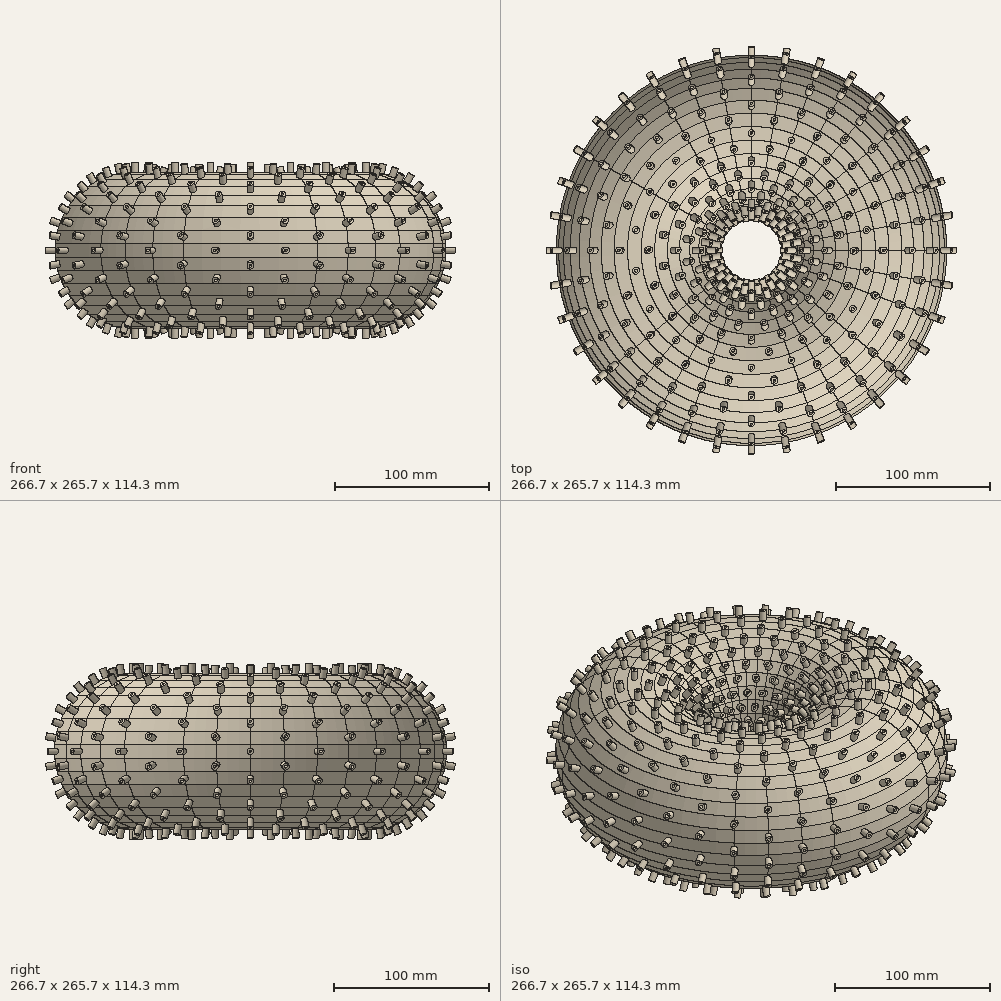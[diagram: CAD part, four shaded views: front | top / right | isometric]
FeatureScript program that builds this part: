
annotation { "Feature Type Name" : "Feature", "Feature Type Description" : "" }
export const myFeature = defineFeature(function(context is Context, id is Id, definition is map)
    precondition{}
    {
        {
            var Q0;
            Q0=qCreatedBy(makeId("Top.planeOp"),FACE);
            var sketch = newSketch(context, id + "F0", { "sketchPlane" : qUnion([Q0])});
            skCircle(sketch, "E0", {"center": v(0, 0) * mm, "radius": 50.8 * mm});
            skSolve(sketch);
        }
        {
            var Q0;
            Q0=qCreatedBy(makeId("Front.planeOp"),FACE);
            cPlane(context, id + "F1", {"entities" : qUnion([Q0]), "cplaneType" : CPlaneType.OFFSET, "offset" : 25.4 * mm, "width" : 152.4 * mm, "height" : 152.4 * mm});
        }
        {
            var Q0;
            Q0=qCreatedBy(id+"F1.planeOp",FACE);
            cPlane(context, id + "F2", {"entities" : qUnion([Q0]), "cplaneType" : CPlaneType.OFFSET, "offset" : 101.6 * mm, "width" : 152.4 * mm, "height" : 152.4 * mm});
        }
        {
            var Q0;
            Q0=qCreatedBy(makeId("Right.planeOp"),FACE);
            var sketch = newSketch(context, id + "F3", { "sketchPlane" : qUnion([Q0])});
            skCircle(sketch, "E1.cCircle", {"center": v(-76.2, 0) * mm, "radius": 50.8 * mm, "construction": true});
            skLineSegment(sketch, "E1.0", {"start": v(-122.42, 21.55) * mm, "end": v(-117.97, 29.25) * mm});
            skLineSegment(sketch, "E1.1", {"start": v(-117.97, 29.25) * mm, "end": v(-112.26, 36.06) * mm});
            skLineSegment(sketch, "E1.2", {"start": v(-112.26, 36.06) * mm, "end": v(-105.45, 41.77) * mm});
            skLineSegment(sketch, "E1.3", {"start": v(-105.45, 41.77) * mm, "end": v(-97.75, 46.22) * mm});
            skLineSegment(sketch, "E1.4", {"start": v(-97.75, 46.22) * mm, "end": v(-89.4, 49.26) * mm});
            skLineSegment(sketch, "E1.5", {"start": v(-89.4, 49.26) * mm, "end": v(-80.64, 50.8) * mm});
            skLineSegment(sketch, "E1.6", {"start": v(-80.64, 50.8) * mm, "end": v(-71.76, 50.8) * mm});
            skLineSegment(sketch, "E1.7", {"start": v(-71.76, 50.8) * mm, "end": v(-63, 49.26) * mm});
            skLineSegment(sketch, "E1.8", {"start": v(-63, 49.26) * mm, "end": v(-54.65, 46.22) * mm});
            skLineSegment(sketch, "E1.9", {"start": v(-54.65, 46.22) * mm, "end": v(-46.95, 41.77) * mm});
            skLineSegment(sketch, "E1.10", {"start": v(-46.95, 41.77) * mm, "end": v(-40.14, 36.06) * mm});
            skLineSegment(sketch, "E1.11", {"start": v(-40.14, 36.06) * mm, "end": v(-34.43, 29.25) * mm});
            skLineSegment(sketch, "E1.12", {"start": v(-34.43, 29.25) * mm, "end": v(-29.98, 21.55) * mm});
            skLineSegment(sketch, "E1.13", {"start": v(-29.98, 21.55) * mm, "end": v(-26.94, 13.2) * mm});
            skLineSegment(sketch, "E1.14", {"start": v(-26.94, 13.2) * mm, "end": v(-25.4, 4.44) * mm});
            skLineSegment(sketch, "E1.15", {"start": v(-25.4, 4.44) * mm, "end": v(-25.4, -4.44) * mm});
            skLineSegment(sketch, "E1.16", {"start": v(-25.4, -4.44) * mm, "end": v(-26.94, -13.2) * mm});
            skLineSegment(sketch, "E1.17", {"start": v(-26.94, -13.2) * mm, "end": v(-29.98, -21.55) * mm});
            skLineSegment(sketch, "E1.18", {"start": v(-29.98, -21.55) * mm, "end": v(-34.43, -29.25) * mm});
            skLineSegment(sketch, "E1.19", {"start": v(-34.43, -29.25) * mm, "end": v(-40.14, -36.06) * mm});
            skLineSegment(sketch, "E1.20", {"start": v(-40.14, -36.06) * mm, "end": v(-46.95, -41.77) * mm});
            skLineSegment(sketch, "E1.21", {"start": v(-46.95, -41.77) * mm, "end": v(-54.65, -46.22) * mm});
            skLineSegment(sketch, "E1.22", {"start": v(-54.65, -46.22) * mm, "end": v(-63, -49.26) * mm});
            skLineSegment(sketch, "E1.23", {"start": v(-63, -49.26) * mm, "end": v(-71.76, -50.8) * mm});
            skLineSegment(sketch, "E1.24", {"start": v(-71.76, -50.8) * mm, "end": v(-80.64, -50.8) * mm});
            skLineSegment(sketch, "E1.25", {"start": v(-80.64, -50.8) * mm, "end": v(-89.4, -49.26) * mm});
            skLineSegment(sketch, "E1.26", {"start": v(-89.4, -49.26) * mm, "end": v(-97.75, -46.22) * mm});
            skLineSegment(sketch, "E1.27", {"start": v(-97.75, -46.22) * mm, "end": v(-105.45, -41.77) * mm});
            skLineSegment(sketch, "E1.28", {"start": v(-105.45, -41.77) * mm, "end": v(-112.26, -36.06) * mm});
            skLineSegment(sketch, "E1.29", {"start": v(-112.26, -36.06) * mm, "end": v(-117.97, -29.25) * mm});
            skLineSegment(sketch, "E1.30", {"start": v(-117.97, -29.25) * mm, "end": v(-122.42, -21.55) * mm});
            skLineSegment(sketch, "E1.31", {"start": v(-122.42, -21.55) * mm, "end": v(-125.46, -13.2) * mm});
            skLineSegment(sketch, "E1.32", {"start": v(-125.46, -13.2) * mm, "end": v(-127, -4.44) * mm});
            skLineSegment(sketch, "E1.33", {"start": v(-127, -4.44) * mm, "end": v(-127, 4.44) * mm});
            skLineSegment(sketch, "E1.34", {"start": v(-127, 4.44) * mm, "end": v(-125.46, 13.2) * mm});
            skLineSegment(sketch, "E1.35", {"start": v(-125.46, 13.2) * mm, "end": v(-122.42, 21.55) * mm});
            skPoint(sketch, "E1.0.midPoint", {"position": v(-120.2, 25.4) * mm});
            skCircle(sketch, "E2.cCircle", {"center": v(-76.2, 0) * mm, "radius": 48.27 * mm, "construction": true});
            skLineSegment(sketch, "E2.0", {"start": v(-124.47, -4.22) * mm, "end": v(-124.47, 4.22) * mm});
            skLineSegment(sketch, "E2.1", {"start": v(-124.47, 4.22) * mm, "end": v(-123, 12.54) * mm});
            skLineSegment(sketch, "E2.2", {"start": v(-123, 12.54) * mm, "end": v(-120.11, 20.48) * mm});
            skLineSegment(sketch, "E2.3", {"start": v(-120.11, 20.48) * mm, "end": v(-115.9, 27.8) * mm});
            skLineSegment(sketch, "E2.4", {"start": v(-115.9, 27.8) * mm, "end": v(-110.46, 34.26) * mm});
            skLineSegment(sketch, "E2.5", {"start": v(-110.46, 34.26) * mm, "end": v(-104, 39.7) * mm});
            skLineSegment(sketch, "E2.6", {"start": v(-104, 39.7) * mm, "end": v(-96.68, 43.91) * mm});
            skLineSegment(sketch, "E2.7", {"start": v(-96.68, 43.91) * mm, "end": v(-88.74, 46.8) * mm});
            skLineSegment(sketch, "E2.8", {"start": v(-88.74, 46.8) * mm, "end": v(-80.42, 48.27) * mm});
            skLineSegment(sketch, "E2.9", {"start": v(-80.42, 48.27) * mm, "end": v(-71.98, 48.27) * mm});
            skLineSegment(sketch, "E2.10", {"start": v(-71.98, 48.27) * mm, "end": v(-63.66, 46.8) * mm});
            skLineSegment(sketch, "E2.11", {"start": v(-63.66, 46.8) * mm, "end": v(-55.72, 43.91) * mm});
            skLineSegment(sketch, "E2.12", {"start": v(-55.72, 43.91) * mm, "end": v(-48.4, 39.7) * mm});
            skLineSegment(sketch, "E2.13", {"start": v(-48.4, 39.7) * mm, "end": v(-41.94, 34.26) * mm});
            skLineSegment(sketch, "E2.14", {"start": v(-41.94, 34.26) * mm, "end": v(-36.5, 27.8) * mm});
            skLineSegment(sketch, "E2.15", {"start": v(-36.5, 27.8) * mm, "end": v(-32.29, 20.48) * mm});
            skLineSegment(sketch, "E2.16", {"start": v(-32.29, 20.48) * mm, "end": v(-29.4, 12.54) * mm});
            skLineSegment(sketch, "E2.17", {"start": v(-29.4, 12.54) * mm, "end": v(-27.93, 4.22) * mm});
            skLineSegment(sketch, "E2.18", {"start": v(-27.93, 4.22) * mm, "end": v(-27.93, -4.22) * mm});
            skLineSegment(sketch, "E2.19", {"start": v(-27.93, -4.22) * mm, "end": v(-29.4, -12.54) * mm});
            skLineSegment(sketch, "E2.20", {"start": v(-29.4, -12.54) * mm, "end": v(-32.29, -20.48) * mm});
            skLineSegment(sketch, "E2.21", {"start": v(-32.29, -20.48) * mm, "end": v(-36.5, -27.8) * mm});
            skLineSegment(sketch, "E2.22", {"start": v(-36.5, -27.8) * mm, "end": v(-41.94, -34.26) * mm});
            skLineSegment(sketch, "E2.23", {"start": v(-41.94, -34.26) * mm, "end": v(-48.4, -39.7) * mm});
            skLineSegment(sketch, "E2.24", {"start": v(-48.4, -39.7) * mm, "end": v(-55.72, -43.91) * mm});
            skLineSegment(sketch, "E2.25", {"start": v(-55.72, -43.91) * mm, "end": v(-63.66, -46.8) * mm});
            skLineSegment(sketch, "E2.26", {"start": v(-63.66, -46.8) * mm, "end": v(-71.98, -48.27) * mm});
            skLineSegment(sketch, "E2.27", {"start": v(-71.98, -48.27) * mm, "end": v(-80.42, -48.27) * mm});
            skLineSegment(sketch, "E2.28", {"start": v(-80.42, -48.27) * mm, "end": v(-88.74, -46.8) * mm});
            skLineSegment(sketch, "E2.29", {"start": v(-88.74, -46.8) * mm, "end": v(-96.68, -43.91) * mm});
            skLineSegment(sketch, "E2.30", {"start": v(-96.68, -43.91) * mm, "end": v(-104, -39.7) * mm});
            skLineSegment(sketch, "E2.31", {"start": v(-104, -39.7) * mm, "end": v(-110.46, -34.26) * mm});
            skLineSegment(sketch, "E2.32", {"start": v(-110.46, -34.26) * mm, "end": v(-115.9, -27.8) * mm});
            skLineSegment(sketch, "E2.33", {"start": v(-115.9, -27.8) * mm, "end": v(-120.11, -20.48) * mm});
            skLineSegment(sketch, "E2.34", {"start": v(-120.11, -20.48) * mm, "end": v(-123, -12.54) * mm});
            skLineSegment(sketch, "E2.35", {"start": v(-123, -12.54) * mm, "end": v(-124.47, -4.22) * mm});
            skPoint(sketch, "E2.0.midPoint", {"position": v(-124.47, 0) * mm});
            skSolve(sketch);
        }
        {
            var Q0;
            Q0=makeQuery(id+"F3.imprint","IMPRINT",FACE,{"disambiguationData":[TD([[makeQuery(id+"F3.imprint","IMPRINT",EDGE,{"derivedFrom":sQuery(id+"F3.wireOp",EDGE,"E1.0")}),-1.0]])]});
            var Q1;
            Q1=sQuery(id+"F0.wireOp",EDGE,"E0");
            revolve(context, id + "F4", {"entities" : qUnion([Q0]), "axis" : qUnion([Q1]), "revolveType" : RevolveType.ONE_DIRECTION, "oppositeDirection" : true, "angle" : 10 * degree});
        }
        {
            var Q0;
            Q0=makeQuery(id+"F4.opRevolve","SWEPT_BODY",BODY,{"disambiguationData":[OSD([sQuery(id+"F3.wireOp",EDGE,"E1.0"),sQuery(id+"F3.wireOp",EDGE,"E1.1"),sQuery(id+"F3.wireOp",EDGE,"E1.2"),sQuery(id+"F3.wireOp",EDGE,"E1.3"),sQuery(id+"F3.wireOp",EDGE,"E1.4"),sQuery(id+"F3.wireOp",EDGE,"E1.5"),sQuery(id+"F3.wireOp",EDGE,"E1.6"),sQuery(id+"F3.wireOp",EDGE,"E1.7"),sQuery(id+"F3.wireOp",EDGE,"E1.8"),sQuery(id+"F3.wireOp",EDGE,"E1.9"),sQuery(id+"F3.wireOp",EDGE,"E1.10"),sQuery(id+"F3.wireOp",EDGE,"E1.11"),sQuery(id+"F3.wireOp",EDGE,"E1.12"),sQuery(id+"F3.wireOp",EDGE,"E1.13"),sQuery(id+"F3.wireOp",EDGE,"E1.14"),sQuery(id+"F3.wireOp",EDGE,"E1.15"),sQuery(id+"F3.wireOp",EDGE,"E1.16"),sQuery(id+"F3.wireOp",EDGE,"E1.17"),sQuery(id+"F3.wireOp",EDGE,"E1.18"),sQuery(id+"F3.wireOp",EDGE,"E1.19"),sQuery(id+"F3.wireOp",EDGE,"E1.20"),sQuery(id+"F3.wireOp",EDGE,"E1.21"),sQuery(id+"F3.wireOp",EDGE,"E1.22"),sQuery(id+"F3.wireOp",EDGE,"E1.23"),sQuery(id+"F3.wireOp",EDGE,"E1.24"),sQuery(id+"F3.wireOp",EDGE,"E1.25"),sQuery(id+"F3.wireOp",EDGE,"E1.26"),sQuery(id+"F3.wireOp",EDGE,"E1.27"),sQuery(id+"F3.wireOp",EDGE,"E1.28"),sQuery(id+"F3.wireOp",EDGE,"E1.29"),sQuery(id+"F3.wireOp",EDGE,"E1.30"),sQuery(id+"F3.wireOp",EDGE,"E1.31"),sQuery(id+"F3.wireOp",EDGE,"E1.32"),sQuery(id+"F3.wireOp",EDGE,"E1.33"),sQuery(id+"F3.wireOp",EDGE,"E1.34"),sQuery(id+"F3.wireOp",EDGE,"E1.35")])]});
            var Q1;
            Q1=sQuery(id+"F0.wireOp",EDGE,"E0");
            circularPattern(context, id + "F5", {"entities" : qUnion([Q0]), "axis" : qUnion([Q1]), "angle" : 10 * degree, "instanceCount" : round(36), "oppositeDirection" : true});
        }
        {
            var Q0;
            Q0=makeQuery(id+"F4.opRevolve","CAP_EDGE",EDGE,{"disambiguationData":[OSD([sQuery(id+"F3.wireOp",EDGE,"E1.34")])],"isStart":true});
            var Q1;
            Q1=sQuery(id+"F0.wireOp",EDGE,"E0");
            cPlane(context, id + "F6", {"entities" : qUnion([Q0, Q1]), "cplaneType" : CPlaneType.LINE_ANGLE, "offset" : 152.4 * mm, "angle" : 90 * degree, "width" : 152.4 * mm, "height" : 152.4 * mm});
        }
        {
            var Q0;
            Q0=qCreatedBy(id+"F6.planeOp",FACE);
            var sketch = newSketch(context, id + "F7", { "sketchPlane" : qUnion([Q0])});
            skCircle(sketch, "E3", {"center": v(0, -13.23) * mm, "radius": 2.22 * mm});
            skCircle(sketch, "E4", {"center": v(0, -13.23) * mm, "radius": 0.95 * mm});
            skSolve(sketch);
        }
        {
            var Q0;
            Q0=makeQuery(id+"F7.imprint","IMPRINT",FACE,{"disambiguationData":[TD([[makeQuery(id+"F7.imprint","IMPRINT",EDGE,{"derivedFrom":sQuery(id+"F7.wireOp",EDGE,"E3")}),1.0]])]});
            extrude(context, id + "F8", {"entities" : qUnion([Q0]), "oppositeDirection" : true, "depth" : 6.35 * mm});
        }
        {
            var Q0;
            Q0=makeQuery(id+"F8.opExtrude","SWEPT_BODY",BODY,{"disambiguationData":[OSD([sQuery(id+"F7.wireOp",EDGE,"E3")])]});
            var Q1;
            Q1=sQuery(id+"F0.wireOp",EDGE,"E0");
            circularPattern(context, id + "F9", {"entities" : qUnion([Q0]), "axis" : qUnion([Q1]), "angle" : 20 * degree, "instanceCount" : round(18), "oppositeDirection" : true});
        }
        {
            var Q0;
            Q0=makeQuery(id+"F5.opPattern","COPY",EDGE,{"derivedFrom":makeQuery(id+"F4.opRevolve","CAP_EDGE",EDGE,{"disambiguationData":[OSD([sQuery(id+"F3.wireOp",EDGE,"E1.35")])],"isStart":true}),"instanceName":"1"});
            var Q1;
            Q1=sQuery(id+"F0.wireOp",EDGE,"E0");
            cPlane(context, id + "F10", {"entities" : qUnion([Q0, Q1]), "cplaneType" : CPlaneType.LINE_ANGLE, "offset" : 152.4 * mm, "angle" : 90 * degree, "width" : 152.4 * mm, "height" : 152.4 * mm});
        }
        {
            var Q0;
            Q0=qCreatedBy(id+"F10.planeOp",FACE);
            var sketch = newSketch(context, id + "F11", { "sketchPlane" : qUnion([Q0])});
            skCircle(sketch, "E5", {"center": v(1.57, -26.01) * mm, "radius": 2.22 * mm});
            skCircle(sketch, "E6", {"center": v(1.57, -26.01) * mm, "radius": 0.95 * mm});
            skSolve(sketch);
        }
        {
            var Q0;
            Q0=makeQuery(id+"F11.imprint","IMPRINT",FACE,{"disambiguationData":[TD([[makeQuery(id+"F11.imprint","IMPRINT",EDGE,{"derivedFrom":sQuery(id+"F11.wireOp",EDGE,"E5")}),1.0]])]});
            extrude(context, id + "F12", {"entities" : qUnion([Q0]), "oppositeDirection" : true, "depth" : 6.35 * mm});
        }
        {
            var Q0;
            Q0=makeQuery(id+"F12.opExtrude","SWEPT_BODY",BODY,{"disambiguationData":[OSD([sQuery(id+"F11.wireOp",EDGE,"E5")])]});
            var Q1;
            Q1=sQuery(id+"F0.wireOp",EDGE,"E0");
            circularPattern(context, id + "F13", {"entities" : qUnion([Q0]), "axis" : qUnion([Q1]), "angle" : 20 * degree, "instanceCount" : round(18)});
        }
        {
            var Q0;
            Q0=makeQuery(id+"F4.opRevolve","CAP_EDGE",EDGE,{"disambiguationData":[OSD([sQuery(id+"F3.wireOp",EDGE,"E1.0")])],"isStart":true});
            var Q1;
            Q1=sQuery(id+"F0.wireOp",EDGE,"E0");
            cPlane(context, id + "F14", {"entities" : qUnion([Q0, Q1]), "cplaneType" : CPlaneType.LINE_ANGLE, "offset" : 152.4 * mm, "angle" : 90 * degree, "width" : 152.4 * mm, "height" : 152.4 * mm});
        }
        {
            var Q0;
            Q0=qCreatedBy(id+"F14.planeOp",FACE);
            var sketch = newSketch(context, id + "F15", { "sketchPlane" : qUnion([Q0])});
            skCircle(sketch, "E7", {"center": v(0, -38.1) * mm, "radius": 2.22 * mm});
            skCircle(sketch, "E8", {"center": v(0, -38.1) * mm, "radius": 0.95 * mm});
            skSolve(sketch);
        }
        {
            var Q0;
            Q0=makeQuery(id+"F15.imprint","IMPRINT",FACE,{"disambiguationData":[TD([[makeQuery(id+"F15.imprint","IMPRINT",EDGE,{"derivedFrom":sQuery(id+"F15.wireOp",EDGE,"E7")}),1.0]])]});
            extrude(context, id + "F16", {"entities" : qUnion([Q0]), "oppositeDirection" : true, "depth" : 6.35 * mm});
        }
        {
            var Q0;
            Q0=makeQuery(id+"F16.opExtrude","SWEPT_BODY",BODY,{"disambiguationData":[OSD([sQuery(id+"F15.wireOp",EDGE,"E7")])]});
            var Q1;
            Q1=sQuery(id+"F0.wireOp",EDGE,"E0");
            circularPattern(context, id + "F17", {"entities" : qUnion([Q0]), "axis" : qUnion([Q1]), "angle" : 20 * degree, "instanceCount" : round(18)});
        }
        {
            var Q0;
            Q0=makeQuery(id+"F5.opPattern","COPY",EDGE,{"derivedFrom":makeQuery(id+"F4.opRevolve","CAP_EDGE",EDGE,{"disambiguationData":[OSD([sQuery(id+"F3.wireOp",EDGE,"E1.1")])],"isStart":false}),"instanceName":"34"});
            var Q1;
            Q1=sQuery(id+"F0.wireOp",EDGE,"E0");
            cPlane(context, id + "F18", {"entities" : qUnion([Q0, Q1]), "cplaneType" : CPlaneType.LINE_ANGLE, "offset" : 152.4 * mm, "angle" : 90 * degree, "width" : 152.4 * mm, "height" : 152.4 * mm});
        }
        {
            var Q0;
            Q0=qCreatedBy(id+"F18.planeOp",FACE);
            var sketch = newSketch(context, id + "F19", { "sketchPlane" : qUnion([Q0])});
            skCircle(sketch, "E9", {"center": v(-5.52, -48.67) * mm, "radius": 2.22 * mm});
            skCircle(sketch, "E10", {"center": v(-5.52, -48.67) * mm, "radius": 0.95 * mm});
            skSolve(sketch);
        }
        {
            var Q0;
            Q0=makeQuery(id+"F19.imprint","IMPRINT",FACE,{"disambiguationData":[TD([[makeQuery(id+"F19.imprint","IMPRINT",EDGE,{"derivedFrom":sQuery(id+"F19.wireOp",EDGE,"E9")}),1.0]])]});
            extrude(context, id + "F20", {"entities" : qUnion([Q0]), "oppositeDirection" : true, "depth" : 6.35 * mm});
        }
        {
            var Q0;
            Q0=makeQuery(id+"F20.opExtrude","SWEPT_BODY",BODY,{"disambiguationData":[OSD([sQuery(id+"F19.wireOp",EDGE,"E9")])]});
            var Q1;
            Q1=sQuery(id+"F0.wireOp",EDGE,"E0");
            circularPattern(context, id + "F21", {"entities" : qUnion([Q0]), "axis" : qUnion([Q1]), "angle" : 20 * degree, "instanceCount" : round(18)});
        }
        {
            var Q0;
            Q0=makeQuery(id+"F4.opRevolve","CAP_EDGE",EDGE,{"disambiguationData":[OSD([sQuery(id+"F3.wireOp",EDGE,"E1.2")])],"isStart":true});
            var Q1;
            Q1=sQuery(id+"F0.wireOp",EDGE,"E0");
            cPlane(context, id + "F22", {"entities" : qUnion([Q0, Q1]), "cplaneType" : CPlaneType.LINE_ANGLE, "offset" : 152.4 * mm, "angle" : 90 * degree, "width" : 152.4 * mm, "height" : 152.4 * mm});
        }
        {
            var Q0;
            Q0=qCreatedBy(id+"F22.planeOp",FACE);
            var sketch = newSketch(context, id + "F23", { "sketchPlane" : qUnion([Q0])});
            skCircle(sketch, "E11", {"center": v(0, 58.37) * mm, "radius": 2.22 * mm});
            skCircle(sketch, "E12", {"center": v(0, 58.37) * mm, "radius": 0.95 * mm});
            skSolve(sketch);
        }
        {
            var Q0;
            Q0=makeQuery(id+"F23.imprint","IMPRINT",FACE,{"disambiguationData":[TD([[makeQuery(id+"F23.imprint","IMPRINT",EDGE,{"derivedFrom":sQuery(id+"F23.wireOp",EDGE,"E11")}),1.0]])]});
            extrude(context, id + "F24", {"entities" : qUnion([Q0]), "oppositeDirection" : true, "depth" : 6.35 * mm});
        }
        {
            var Q0;
            Q0=makeQuery(id+"F24.opExtrude","SWEPT_BODY",BODY,{"disambiguationData":[OSD([sQuery(id+"F23.wireOp",EDGE,"E11")])]});
            var Q1;
            Q1=sQuery(id+"F0.wireOp",EDGE,"E0");
            circularPattern(context, id + "F25", {"entities" : qUnion([Q0]), "axis" : qUnion([Q1]), "angle" : 20 * degree, "instanceCount" : round(18)});
        }
        {
            var Q0;
            Q0=makeQuery(id+"F5.opPattern","COPY",EDGE,{"derivedFrom":makeQuery(id+"F4.opRevolve","CAP_EDGE",EDGE,{"disambiguationData":[OSD([sQuery(id+"F3.wireOp",EDGE,"E1.3")])],"isStart":true}),"instanceName":"1"});
            var Q1;
            Q1=sQuery(id+"F0.wireOp",EDGE,"E0");
            cPlane(context, id + "F26", {"entities" : qUnion([Q0, Q1]), "cplaneType" : CPlaneType.LINE_ANGLE, "offset" : 152.4 * mm, "angle" : 90 * degree, "width" : 152.4 * mm, "height" : 152.4 * mm});
        }
        {
            var Q0;
            Q0=qCreatedBy(id+"F26.planeOp",FACE);
            var sketch = newSketch(context, id + "F27", { "sketchPlane" : qUnion([Q0])});
            skCircle(sketch, "E13", {"center": v(-9.96, 65.23) * mm, "radius": 2.22 * mm});
            skCircle(sketch, "E14", {"center": v(-9.96, 65.23) * mm, "radius": 0.95 * mm});
            skSolve(sketch);
        }
        {
            var Q0;
            Q0=qSketchRegion(id+"F27",true);
            extrude(context, id + "F28", {"entities" : qUnion([Q0]), "oppositeDirection" : true, "depth" : 6.35 * mm});
        }
        {
            var Q0;
            Q0=makeQuery(id+"F28.opExtrude","SWEPT_BODY",BODY,{"disambiguationData":[OSD([sQuery(id+"F27.wireOp",EDGE,"E13")])]});
            var Q1;
            Q1=sQuery(id+"F0.wireOp",EDGE,"E0");
            circularPattern(context, id + "F29", {"entities" : qUnion([Q0]), "axis" : qUnion([Q1]), "angle" : 20 * degree, "instanceCount" : round(18)});
        }
        {
            var Q0;
            Q0=makeQuery(id+"F4.opRevolve","CAP_EDGE",EDGE,{"disambiguationData":[OSD([sQuery(id+"F3.wireOp",EDGE,"E1.4")])],"isStart":true});
            var Q1;
            Q1=sQuery(id+"F0.wireOp",EDGE,"E0");
            cPlane(context, id + "F30", {"entities" : qUnion([Q0, Q1]), "cplaneType" : CPlaneType.LINE_ANGLE, "offset" : 152.4 * mm, "angle" : 90 * degree, "width" : 152.4 * mm, "height" : 152.4 * mm});
        }
        {
            var Q0;
            Q0=qCreatedBy(id+"F30.planeOp",FACE);
            var sketch = newSketch(context, id + "F31", { "sketchPlane" : qUnion([Q0])});
            skCircle(sketch, "E15", {"center": v(0, 71.6) * mm, "radius": 2.22 * mm});
            skCircle(sketch, "E16", {"center": v(0, 71.6) * mm, "radius": 0.95 * mm});
            skSolve(sketch);
        }
        {
            var Q0;
            Q0=qSketchRegion(id+"F31",true);
            extrude(context, id + "F32", {"entities" : qUnion([Q0]), "oppositeDirection" : true, "depth" : 6.35 * mm});
        }
        {
            var Q0;
            Q0=makeQuery(id+"F32.opExtrude","SWEPT_BODY",BODY,{"disambiguationData":[OSD([sQuery(id+"F31.wireOp",EDGE,"E15")])]});
            var Q1;
            Q1=sQuery(id+"F0.wireOp",EDGE,"E0");
            circularPattern(context, id + "F33", {"entities" : qUnion([Q0]), "axis" : qUnion([Q1]), "angle" : 20 * degree, "instanceCount" : round(18)});
        }
        {
            var Q0;
            Q0=makeQuery(id+"F5.opPattern","COPY",EDGE,{"derivedFrom":makeQuery(id+"F4.opRevolve","CAP_EDGE",EDGE,{"disambiguationData":[OSD([sQuery(id+"F3.wireOp",EDGE,"E1.5")])],"isStart":true}),"instanceName":"1"});
            var Q1;
            Q1=sQuery(id+"F0.wireOp",EDGE,"E0");
            cPlane(context, id + "F34", {"entities" : qUnion([Q0, Q1]), "cplaneType" : CPlaneType.LINE_ANGLE, "offset" : 152.4 * mm, "angle" : 90 * degree, "width" : 152.4 * mm, "height" : 152.4 * mm});
        }
        {
            var Q0;
            Q0=qCreatedBy(id+"F34.planeOp",FACE);
            var sketch = newSketch(context, id + "F35", { "sketchPlane" : qUnion([Q0])});
            skCircle(sketch, "E17", {"center": v(-12.84, 73.94) * mm, "radius": 2.22 * mm});
            skCircle(sketch, "E18", {"center": v(-12.84, 73.94) * mm, "radius": 0.95 * mm});
            skSolve(sketch);
        }
        {
            var Q0;
            Q0=qSketchRegion(id+"F35",true);
            extrude(context, id + "F36", {"entities" : qUnion([Q0]), "oppositeDirection" : true, "depth" : 6.35 * mm});
        }
        {
            var Q0;
            Q0=makeQuery(id+"F36.opExtrude","SWEPT_BODY",BODY,{"disambiguationData":[OSD([sQuery(id+"F35.wireOp",EDGE,"E17")])]});
            var Q1;
            Q1=sQuery(id+"F0.wireOp",EDGE,"E0");
            circularPattern(context, id + "F37", {"entities" : qUnion([Q0]), "axis" : qUnion([Q1]), "angle" : 20 * degree, "instanceCount" : round(18)});
        }
        {
            var Q0;
            Q0=makeQuery(id+"F4.opRevolve","CAP_EDGE",EDGE,{"disambiguationData":[OSD([sQuery(id+"F3.wireOp",EDGE,"E1.6")])],"isStart":true});
            var Q1;
            Q1=sQuery(id+"F0.wireOp",EDGE,"E0");
            cPlane(context, id + "F38", {"entities" : qUnion([Q0, Q1]), "cplaneType" : CPlaneType.LINE_ANGLE, "offset" : 152.4 * mm, "angle" : 90 * degree, "width" : 152.4 * mm, "height" : 152.4 * mm});
        }
        {
            var Q0;
            Q0=qCreatedBy(id+"F38.planeOp",FACE);
            var sketch = newSketch(context, id + "F39", { "sketchPlane" : qUnion([Q0])});
            skCircle(sketch, "E19", {"center": v(0, 76.2) * mm, "radius": 2.22 * mm});
            skCircle(sketch, "E20", {"center": v(0, 76.2) * mm, "radius": 0.95 * mm});
            skSolve(sketch);
        }
        {
            var Q0;
            Q0=qSketchRegion(id+"F39",true);
            extrude(context, id + "F40", {"entities" : qUnion([Q0]), "oppositeDirection" : true, "depth" : 6.35 * mm});
        }
        {
            var Q0;
            Q0=makeQuery(id+"F40.opExtrude","SWEPT_BODY",BODY,{"disambiguationData":[OSD([sQuery(id+"F39.wireOp",EDGE,"E19")])]});
            var Q1;
            Q1=sQuery(id+"F0.wireOp",EDGE,"E0");
            circularPattern(context, id + "F41", {"entities" : qUnion([Q0]), "axis" : qUnion([Q1]), "angle" : 20 * degree, "instanceCount" : round(18)});
        }
        {
            var Q0;
            Q0=makeQuery(id+"F5.opPattern","COPY",EDGE,{"derivedFrom":makeQuery(id+"F4.opRevolve","CAP_EDGE",EDGE,{"disambiguationData":[OSD([sQuery(id+"F3.wireOp",EDGE,"E1.7")])],"isStart":false}),"instanceName":"34"});
            var Q1;
            Q1=sQuery(id+"F0.wireOp",EDGE,"E0");
            cPlane(context, id + "F42", {"entities" : qUnion([Q0, Q1]), "cplaneType" : CPlaneType.LINE_ANGLE, "offset" : 152.4 * mm, "angle" : 90 * degree, "width" : 152.4 * mm, "height" : 152.4 * mm});
        }
        {
            var Q0;
            Q0=qCreatedBy(id+"F42.planeOp",FACE);
            var sketch = newSketch(context, id + "F43", { "sketchPlane" : qUnion([Q0])});
            skCircle(sketch, "E21", {"center": v(-10.55, 73.94) * mm, "radius": 2.22 * mm});
            skCircle(sketch, "E22", {"center": v(-10.55, 73.94) * mm, "radius": 0.95 * mm});
            skSolve(sketch);
        }
        {
            var Q0;
            Q0=qSketchRegion(id+"F43",true);
            extrude(context, id + "F44", {"entities" : qUnion([Q0]), "oppositeDirection" : true, "depth" : 6.35 * mm});
        }
        {
            var Q0;
            Q0=makeQuery(id+"F44.opExtrude","SWEPT_BODY",BODY,{"disambiguationData":[OSD([sQuery(id+"F43.wireOp",EDGE,"E21")])]});
            var Q1;
            Q1=sQuery(id+"F0.wireOp",EDGE,"E0");
            circularPattern(context, id + "F45", {"entities" : qUnion([Q0]), "axis" : qUnion([Q1]), "angle" : 20 * degree, "instanceCount" : round(18)});
        }
        {
            var Q0;
            Q0=makeQuery(id+"F4.opRevolve","CAP_EDGE",EDGE,{"disambiguationData":[OSD([sQuery(id+"F3.wireOp",EDGE,"E1.8")])],"isStart":true});
            var Q1;
            Q1=sQuery(id+"F0.wireOp",EDGE,"E0");
            cPlane(context, id + "F46", {"entities" : qUnion([Q0, Q1]), "cplaneType" : CPlaneType.LINE_ANGLE, "offset" : 152.4 * mm, "angle" : 90 * degree, "width" : 152.4 * mm, "height" : 152.4 * mm});
        }
        {
            var Q0;
            Q0=qCreatedBy(id+"F46.planeOp",FACE);
            var sketch = newSketch(context, id + "F47", { "sketchPlane" : qUnion([Q0])});
            skCircle(sketch, "E23", {"center": v(0, 71.6) * mm, "radius": 2.22 * mm});
            skCircle(sketch, "E24", {"center": v(0, 71.6) * mm, "radius": 0.95 * mm});
            skSolve(sketch);
        }
        {
            var Q0;
            Q0=qSketchRegion(id+"F47",true);
            extrude(context, id + "F48", {"entities" : qUnion([Q0]), "oppositeDirection" : true, "depth" : 6.35 * mm});
        }
        {
            var Q0;
            Q0=makeQuery(id+"F48.opExtrude","SWEPT_BODY",BODY,{"disambiguationData":[OSD([sQuery(id+"F47.wireOp",EDGE,"E23")])]});
            var Q1;
            Q1=sQuery(id+"F0.wireOp",EDGE,"E0");
            circularPattern(context, id + "F49", {"entities" : qUnion([Q0]), "axis" : qUnion([Q1]), "angle" : 20 * degree, "instanceCount" : round(18)});
        }
        {
            var Q0;
            Q0=makeQuery(id+"F5.opPattern","COPY",EDGE,{"derivedFrom":makeQuery(id+"F4.opRevolve","CAP_EDGE",EDGE,{"disambiguationData":[OSD([sQuery(id+"F3.wireOp",EDGE,"E1.9")])],"isStart":false}),"instanceName":"6"});
            var Q1;
            Q1=sQuery(id+"F0.wireOp",EDGE,"E0");
            cPlane(context, id + "F50", {"entities" : qUnion([Q0, Q1]), "cplaneType" : CPlaneType.LINE_ANGLE, "offset" : 152.4 * mm, "angle" : 90 * degree, "width" : 152.4 * mm, "height" : 152.4 * mm});
        }
        {
            var Q0;
            Q0=qCreatedBy(id+"F50.planeOp",FACE);
            var sketch = newSketch(context, id + "F51", { "sketchPlane" : qUnion([Q0])});
            skCircle(sketch, "E25", {"center": v(-60.84, 25.57) * mm, "radius": 2.22 * mm});
            skCircle(sketch, "E26", {"center": v(-60.84, 25.57) * mm, "radius": 0.95 * mm});
            skSolve(sketch);
        }
        {
            var Q0;
            Q0=qSketchRegion(id+"F51",true);
            extrude(context, id + "F52", {"entities" : qUnion([Q0]), "oppositeDirection" : true, "depth" : 6.35 * mm});
        }
        {
            var Q0;
            Q0=makeQuery(id+"F52.opExtrude","SWEPT_BODY",BODY,{"disambiguationData":[OSD([sQuery(id+"F51.wireOp",EDGE,"E25")])]});
            var Q1;
            Q1=sQuery(id+"F0.wireOp",EDGE,"E0");
            circularPattern(context, id + "F53", {"entities" : qUnion([Q0]), "axis" : qUnion([Q1]), "angle" : 20 * degree, "instanceCount" : round(18)});
        }
        {
            var Q0;
            Q0=makeQuery(id+"F5.opPattern","COPY",EDGE,{"derivedFrom":makeQuery(id+"F4.opRevolve","CAP_EDGE",EDGE,{"disambiguationData":[OSD([sQuery(id+"F3.wireOp",EDGE,"E1.10")])],"isStart":false}),"instanceName":"7"});
            var Q1;
            Q1=sQuery(id+"F0.wireOp",EDGE,"E0");
            cPlane(context, id + "F54", {"entities" : qUnion([Q0, Q1]), "cplaneType" : CPlaneType.LINE_ANGLE, "offset" : 152.4 * mm, "angle" : 90 * degree, "width" : 152.4 * mm, "height" : 152.4 * mm});
        }
        {
            var Q0;
            Q0=qCreatedBy(id+"F54.planeOp",FACE);
            var sketch = newSketch(context, id + "F55", { "sketchPlane" : qUnion([Q0])});
            skCircle(sketch, "E27", {"center": v(-56.89, 13.1) * mm, "radius": 2.22 * mm});
            skCircle(sketch, "E28", {"center": v(-56.89, 13.1) * mm, "radius": 0.95 * mm});
            skSolve(sketch);
        }
        {
            var Q0;
            Q0=qSketchRegion(id+"F55",true);
            extrude(context, id + "F56", {"entities" : qUnion([Q0]), "oppositeDirection" : true, "depth" : 6.35 * mm});
        }
        {
            var Q0;
            Q0=makeQuery(id+"F56.opExtrude","SWEPT_BODY",BODY,{"disambiguationData":[OSD([sQuery(id+"F55.wireOp",EDGE,"E27")])]});
            var Q1;
            Q1=sQuery(id+"F0.wireOp",EDGE,"E0");
            circularPattern(context, id + "F57", {"entities" : qUnion([Q0]), "axis" : qUnion([Q1]), "angle" : 20 * degree, "instanceCount" : round(18)});
        }
        {
            var Q0;
            Q0=makeQuery(id+"F5.opPattern","COPY",EDGE,{"derivedFrom":makeQuery(id+"F4.opRevolve","CAP_EDGE",EDGE,{"disambiguationData":[OSD([sQuery(id+"F3.wireOp",EDGE,"E1.11")])],"isStart":false}),"instanceName":"8"});
            var Q1;
            Q1=sQuery(id+"F0.wireOp",EDGE,"E0");
            cPlane(context, id + "F58", {"entities" : qUnion([Q0, Q1]), "cplaneType" : CPlaneType.LINE_ANGLE, "offset" : 152.4 * mm, "angle" : 90 * degree, "width" : 152.4 * mm, "height" : 152.4 * mm});
        }
        {
            var Q0;
            Q0=qCreatedBy(id+"F58.planeOp",FACE);
            var sketch = newSketch(context, id + "F59", { "sketchPlane" : qUnion([Q0])});
            skCircle(sketch, "E29", {"center": v(0, 48.98) * mm, "radius": 2.22 * mm});
            skCircle(sketch, "E30", {"center": v(0, 48.98) * mm, "radius": 0.95 * mm});
            skSolve(sketch);
        }
        {
            var Q0;
            Q0=qSketchRegion(id+"F59",true);
            extrude(context, id + "F60", {"entities" : qUnion([Q0]), "oppositeDirection" : true, "depth" : 6.35 * mm});
        }
        {
            var Q0;
            Q0=makeQuery(id+"F60.opExtrude","SWEPT_BODY",BODY,{"disambiguationData":[OSD([sQuery(id+"F59.wireOp",EDGE,"E29")])]});
            var Q1;
            Q1=sQuery(id+"F0.wireOp",EDGE,"E0");
            circularPattern(context, id + "F61", {"entities" : qUnion([Q0]), "axis" : qUnion([Q1]), "angle" : 20 * degree, "instanceCount" : round(18)});
        }
        {
            var Q0;
            Q0=makeQuery(id+"F5.opPattern","COPY",EDGE,{"derivedFrom":makeQuery(id+"F4.opRevolve","CAP_EDGE",EDGE,{"disambiguationData":[OSD([sQuery(id+"F3.wireOp",EDGE,"E1.12")])],"isStart":false}),"instanceName":"5"});
            var Q1;
            Q1=sQuery(id+"F0.wireOp",EDGE,"E0");
            cPlane(context, id + "F62", {"entities" : qUnion([Q0, Q1]), "cplaneType" : CPlaneType.LINE_ANGLE, "offset" : 152.4 * mm, "angle" : 90 * degree, "width" : 152.4 * mm, "height" : 152.4 * mm});
        }
        {
            var Q0;
            Q0=qCreatedBy(id+"F62.planeOp",FACE);
            var sketch = newSketch(context, id + "F63", { "sketchPlane" : qUnion([Q0])});
            skCircle(sketch, "E31", {"center": v(10.57, 36.6) * mm, "radius": 2.22 * mm});
            skCircle(sketch, "E32", {"center": v(10.57, 36.6) * mm, "radius": 0.95 * mm});
            skSolve(sketch);
        }
        {
            var Q0;
            Q0=qSketchRegion(id+"F63",true);
            extrude(context, id + "F64", {"entities" : qUnion([Q0]), "oppositeDirection" : true, "depth" : 6.35 * mm});
        }
        {
            var Q0;
            Q0=makeQuery(id+"F64.opExtrude","SWEPT_BODY",BODY,{"disambiguationData":[OSD([sQuery(id+"F63.wireOp",EDGE,"E31")])]});
            var Q1;
            Q1=sQuery(id+"F0.wireOp",EDGE,"E0");
            circularPattern(context, id + "F65", {"entities" : qUnion([Q0]), "axis" : qUnion([Q1]), "angle" : 20 * degree, "instanceCount" : round(18)});
        }
        {
            var Q0;
            Q0=makeQuery(id+"F5.opPattern","COPY",EDGE,{"derivedFrom":makeQuery(id+"F4.opRevolve","CAP_EDGE",EDGE,{"disambiguationData":[OSD([sQuery(id+"F3.wireOp",EDGE,"E1.13")])],"isStart":false}),"instanceName":"8"});
            var Q1;
            Q1=sQuery(id+"F0.wireOp",EDGE,"E0");
            cPlane(context, id + "F66", {"entities" : qUnion([Q0, Q1]), "cplaneType" : CPlaneType.LINE_ANGLE, "offset" : 152.4 * mm, "angle" : 90 * degree, "width" : 152.4 * mm, "height" : 152.4 * mm});
        }
        {
            var Q0;
            Q0=qCreatedBy(id+"F66.planeOp",FACE);
            var sketch = newSketch(context, id + "F67", { "sketchPlane" : qUnion([Q0])});
            skCircle(sketch, "E33", {"center": v(0, 26.06) * mm, "radius": 2.22 * mm});
            skCircle(sketch, "E34", {"center": v(0, 26.06) * mm, "radius": 0.95 * mm});
            skSolve(sketch);
        }
        {
            var Q0;
            Q0=qSketchRegion(id+"F67",true);
            extrude(context, id + "F68", {"entities" : qUnion([Q0]), "oppositeDirection" : true, "depth" : 6.35 * mm});
        }
        {
            var Q0;
            Q0=makeQuery(id+"F68.opExtrude","SWEPT_BODY",BODY,{"disambiguationData":[OSD([sQuery(id+"F67.wireOp",EDGE,"E33")])]});
            var Q1;
            Q1=sQuery(id+"F0.wireOp",EDGE,"E0");
            circularPattern(context, id + "F69", {"entities" : qUnion([Q0]), "axis" : qUnion([Q1]), "angle" : 20 * degree, "instanceCount" : round(18)});
        }
        {
            var Q0;
            Q0=makeQuery(id+"F5.opPattern","COPY",EDGE,{"derivedFrom":makeQuery(id+"F4.opRevolve","CAP_EDGE",EDGE,{"disambiguationData":[OSD([sQuery(id+"F3.wireOp",EDGE,"E1.14")])],"isStart":false}),"instanceName":"7"});
            var Q1;
            Q1=sQuery(id+"F0.wireOp",EDGE,"E0");
            cPlane(context, id + "F70", {"entities" : qUnion([Q0, Q1]), "cplaneType" : CPlaneType.LINE_ANGLE, "offset" : 152.4 * mm, "angle" : 90 * degree, "width" : 152.4 * mm, "height" : 152.4 * mm});
        }
        {
            var Q0;
            Q0=qCreatedBy(id+"F70.planeOp",FACE);
            var sketch = newSketch(context, id + "F71", { "sketchPlane" : qUnion([Q0])});
            skCircle(sketch, "E35", {"center": v(0.4, 13.23) * mm, "radius": 2.22 * mm});
            skCircle(sketch, "E36", {"center": v(0.4, 13.23) * mm, "radius": 0.95 * mm});
            skSolve(sketch);
        }
        {
            var Q0;
            Q0=qSketchRegion(id+"F71",true);
            extrude(context, id + "F72", {"entities" : qUnion([Q0]), "oppositeDirection" : true, "depth" : 6.35 * mm});
        }
        {
            var Q0;
            Q0=makeQuery(id+"F72.opExtrude","SWEPT_BODY",BODY,{"disambiguationData":[OSD([sQuery(id+"F71.wireOp",EDGE,"E35")])]});
            var Q1;
            Q1=sQuery(id+"F0.wireOp",EDGE,"E0");
            circularPattern(context, id + "F73", {"entities" : qUnion([Q0]), "axis" : qUnion([Q1]), "angle" : 20 * degree, "instanceCount" : round(18)});
        }
        {
            var Q0;
            Q0=makeQuery(id+"F5.opPattern","COPY",EDGE,{"derivedFrom":makeQuery(id+"F4.opRevolve","CAP_EDGE",EDGE,{"disambiguationData":[OSD([sQuery(id+"F3.wireOp",EDGE,"E1.15")])],"isStart":false}),"instanceName":"8"});
            var Q1;
            Q1=sQuery(id+"F0.wireOp",EDGE,"E0");
            cPlane(context, id + "F74", {"entities" : qUnion([Q0, Q1]), "cplaneType" : CPlaneType.LINE_ANGLE, "offset" : 152.4 * mm, "angle" : 90 * degree, "width" : 152.4 * mm, "height" : 152.4 * mm});
        }
        {
            var Q0;
            Q0=qCreatedBy(id+"F74.planeOp",FACE);
            var sketch = newSketch(context, id + "F75", { "sketchPlane" : qUnion([Q0])});
            skCircle(sketch, "E37", {"center": v(0, 0) * mm, "radius": 2.22 * mm});
            skCircle(sketch, "E38", {"center": v(0, 0) * mm, "radius": 0.95 * mm});
            skSolve(sketch);
        }
        {
            var Q0;
            Q0=qSketchRegion(id+"F75",true);
            extrude(context, id + "F76", {"entities" : qUnion([Q0]), "oppositeDirection" : true, "depth" : 6.35 * mm});
        }
        {
            var Q0;
            Q0=makeQuery(id+"F76.opExtrude","SWEPT_BODY",BODY,{"disambiguationData":[OSD([sQuery(id+"F75.wireOp",EDGE,"E37")])]});
            var Q1;
            Q1=sQuery(id+"F0.wireOp",EDGE,"E0");
            circularPattern(context, id + "F77", {"entities" : qUnion([Q0]), "axis" : qUnion([Q1]), "angle" : 20 * degree, "instanceCount" : round(18)});
        }
        {
            var Q0;
            Q0=makeQuery(id+"F5.opPattern","COPY",EDGE,{"derivedFrom":makeQuery(id+"F4.opRevolve","CAP_EDGE",EDGE,{"disambiguationData":[OSD([sQuery(id+"F3.wireOp",EDGE,"E1.16")])],"isStart":true}),"instanceName":"10"});
            var Q1;
            Q1=sQuery(id+"F0.wireOp",EDGE,"E0");
            cPlane(context, id + "F78", {"entities" : qUnion([Q0, Q1]), "cplaneType" : CPlaneType.LINE_ANGLE, "offset" : 152.4 * mm, "angle" : 90 * degree, "width" : 152.4 * mm, "height" : 152.4 * mm});
        }
        {
            var Q0;
            Q0=qCreatedBy(id+"F78.planeOp",FACE);
            var sketch = newSketch(context, id + "F79", { "sketchPlane" : qUnion([Q0])});
            skCircle(sketch, "E39", {"center": v(0.4, -13.23) * mm, "radius": 2.22 * mm});
            skCircle(sketch, "E40", {"center": v(0.4, -13.23) * mm, "radius": 0.95 * mm});
            skSolve(sketch);
        }
        {
            var Q0;
            Q0=qSketchRegion(id+"F79",true);
            extrude(context, id + "F80", {"entities" : qUnion([Q0]), "depth" : 6.35 * mm});
        }
        {
            var Q0;
            Q0=makeQuery(id+"F80.opExtrude","SWEPT_BODY",BODY,{"disambiguationData":[OSD([sQuery(id+"F79.wireOp",EDGE,"E39")])]});
            var Q1;
            Q1=sQuery(id+"F0.wireOp",EDGE,"E0");
            circularPattern(context, id + "F81", {"entities" : qUnion([Q0]), "axis" : qUnion([Q1]), "angle" : 20 * degree, "instanceCount" : round(18)});
        }
        {
            var Q0;
            Q0=makeQuery(id+"F5.opPattern","COPY",EDGE,{"derivedFrom":makeQuery(id+"F4.opRevolve","CAP_EDGE",EDGE,{"disambiguationData":[OSD([sQuery(id+"F3.wireOp",EDGE,"E1.17")])],"isStart":true}),"instanceName":"11"});
            var Q1;
            Q1=sQuery(id+"F0.wireOp",EDGE,"E0");
            cPlane(context, id + "F82", {"entities" : qUnion([Q0, Q1]), "cplaneType" : CPlaneType.LINE_ANGLE, "offset" : 152.4 * mm, "angle" : 90 * degree, "width" : 152.4 * mm, "height" : 152.4 * mm});
        }
        {
            var Q0;
            Q0=qCreatedBy(id+"F82.planeOp",FACE);
            var sketch = newSketch(context, id + "F83", { "sketchPlane" : qUnion([Q0])});
            skCircle(sketch, "E41", {"center": v(3.22, -25.86) * mm, "radius": 2.22 * mm});
            skCircle(sketch, "E42", {"center": v(3.22, -25.86) * mm, "radius": 0.95 * mm});
            skSolve(sketch);
        }
        {
            var Q0;
            Q0=qSketchRegion(id+"F83",true);
            extrude(context, id + "F84", {"entities" : qUnion([Q0]), "depth" : 6.35 * mm});
        }
        {
            var Q0;
            Q0=makeQuery(id+"F84.opExtrude","SWEPT_BODY",BODY,{"disambiguationData":[OSD([sQuery(id+"F83.wireOp",EDGE,"E41")])]});
            var Q1;
            Q1=sQuery(id+"F0.wireOp",EDGE,"E0");
            circularPattern(context, id + "F85", {"entities" : qUnion([Q0]), "axis" : qUnion([Q1]), "angle" : 20 * degree, "instanceCount" : round(18)});
        }
        {
            var Q0;
            Q0=makeQuery(id+"F5.opPattern","COPY",EDGE,{"derivedFrom":makeQuery(id+"F4.opRevolve","CAP_EDGE",EDGE,{"disambiguationData":[OSD([sQuery(id+"F3.wireOp",EDGE,"E1.33")])],"isStart":true}),"instanceName":"13"});
            var Q1;
            Q1=sQuery(id+"F0.wireOp",EDGE,"E0");
            cPlane(context, id + "F86", {"entities" : qUnion([Q0, Q1]), "cplaneType" : CPlaneType.LINE_ANGLE, "offset" : 152.4 * mm, "angle" : 90 * degree, "width" : 152.4 * mm, "height" : 152.4 * mm});
        }
        {
            var Q0;
            Q0=qCreatedBy(id+"F86.planeOp",FACE);
            var sketch = newSketch(context, id + "F87", { "sketchPlane" : qUnion([Q0])});
            skCircle(sketch, "E43", {"center": v(0, 0) * mm, "radius": 2.22 * mm});
            skCircle(sketch, "E44", {"center": v(0, 0) * mm, "radius": 0.95 * mm});
            skSolve(sketch);
        }
        {
            var Q0;
            Q0=qSketchRegion(id+"F87",true);
            extrude(context, id + "F88", {"entities" : qUnion([Q0]), "depth" : 6.35 * mm});
        }
        {
            var Q0;
            Q0=makeQuery(id+"F88.opExtrude","SWEPT_BODY",BODY,{"disambiguationData":[OSD([sQuery(id+"F87.wireOp",EDGE,"E43")])]});
            var Q1;
            Q1=sQuery(id+"F0.wireOp",EDGE,"E0");
            circularPattern(context, id + "F89", {"entities" : qUnion([Q0]), "axis" : qUnion([Q1]), "angle" : 20 * degree, "instanceCount" : round(18)});
        }
        {
            var Q0;
            Q0=makeQuery(id+"F5.opPattern","COPY",EDGE,{"derivedFrom":makeQuery(id+"F4.opRevolve","CAP_EDGE",EDGE,{"disambiguationData":[OSD([sQuery(id+"F3.wireOp",EDGE,"E1.32")])],"isStart":false}),"instanceName":"13"});
            var Q1;
            Q1=sQuery(id+"F0.wireOp",EDGE,"E0");
            cPlane(context, id + "F90", {"entities" : qUnion([Q0, Q1]), "cplaneType" : CPlaneType.LINE_ANGLE, "offset" : 152.4 * mm, "angle" : 90 * degree, "width" : 152.4 * mm, "height" : 152.4 * mm});
        }
        {
            var Q0;
            Q0=qCreatedBy(id+"F90.planeOp",FACE);
            var sketch = newSketch(context, id + "F91", { "sketchPlane" : qUnion([Q0])});
            skCircle(sketch, "E45", {"center": v(1.9, 13.1) * mm, "radius": 2.22 * mm});
            skCircle(sketch, "E46", {"center": v(1.9, 13.1) * mm, "radius": 0.95 * mm});
            skSolve(sketch);
        }
        {
            var Q0;
            Q0=qSketchRegion(id+"F91",true);
            extrude(context, id + "F92", {"entities" : qUnion([Q0]), "depth" : 6.35 * mm});
        }
        {
            var Q0;
            Q0=makeQuery(id+"F92.opExtrude","SWEPT_BODY",BODY,{"disambiguationData":[OSD([sQuery(id+"F91.wireOp",EDGE,"E45")])]});
            var Q1;
            Q1=sQuery(id+"F0.wireOp",EDGE,"E0");
            circularPattern(context, id + "F93", {"entities" : qUnion([Q0]), "axis" : qUnion([Q1]), "angle" : 20 * degree, "instanceCount" : round(18)});
        }
        {
            var Q0;
            Q0=makeQuery(id+"F5.opPattern","COPY",EDGE,{"derivedFrom":makeQuery(id+"F4.opRevolve","CAP_EDGE",EDGE,{"disambiguationData":[OSD([sQuery(id+"F3.wireOp",EDGE,"E1.31")])],"isStart":true}),"instanceName":"13"});
            var Q1;
            Q1=sQuery(id+"F0.wireOp",EDGE,"E0");
            cPlane(context, id + "F94", {"entities" : qUnion([Q0, Q1]), "cplaneType" : CPlaneType.LINE_ANGLE, "offset" : 152.4 * mm, "angle" : 90 * degree, "width" : 152.4 * mm, "height" : 152.4 * mm});
        }
        {
            var Q0;
            Q0=qCreatedBy(id+"F94.planeOp",FACE);
            var sketch = newSketch(context, id + "F95", { "sketchPlane" : qUnion([Q0])});
            skCircle(sketch, "E47", {"center": v(-7.19, 25.05) * mm, "radius": 2.22 * mm});
            skCircle(sketch, "E48", {"center": v(-7.19, 25.05) * mm, "radius": 0.95 * mm});
            skSolve(sketch);
        }
        {
            var Q0;
            Q0=qSketchRegion(id+"F95",true);
            extrude(context, id + "F96", {"entities" : qUnion([Q0]), "depth" : 6.35 * mm});
        }
        {
            var Q0;
            Q0=makeQuery(id+"F96.opExtrude","SWEPT_BODY",BODY,{"disambiguationData":[OSD([sQuery(id+"F95.wireOp",EDGE,"E47")])]});
            var Q1;
            Q1=sQuery(id+"F0.wireOp",EDGE,"E0");
            circularPattern(context, id + "F97", {"entities" : qUnion([Q0]), "axis" : qUnion([Q1]), "angle" : 20 * degree, "instanceCount" : round(18)});
        }
        {
            var Q0;
            Q0=makeQuery(id+"F5.opPattern","COPY",EDGE,{"derivedFrom":makeQuery(id+"F4.opRevolve","CAP_EDGE",EDGE,{"disambiguationData":[OSD([sQuery(id+"F3.wireOp",EDGE,"E1.30")])],"isStart":false}),"instanceName":"13"});
            var Q1;
            Q1=sQuery(id+"F0.wireOp",EDGE,"E0");
            cPlane(context, id + "F98", {"entities" : qUnion([Q0, Q1]), "cplaneType" : CPlaneType.LINE_ANGLE, "offset" : 152.4 * mm, "angle" : 90 * degree, "width" : 152.4 * mm, "height" : 152.4 * mm});
        }
        {
            var Q0;
            Q0=qCreatedBy(id+"F98.planeOp",FACE);
            var sketch = newSketch(context, id + "F99", { "sketchPlane" : qUnion([Q0])});
            skCircle(sketch, "E49", {"center": v(14.74, 35.13) * mm, "radius": 2.22 * mm});
            skCircle(sketch, "E50", {"center": v(14.74, 35.13) * mm, "radius": 0.95 * mm});
            skSolve(sketch);
        }
        {
            var Q0;
            Q0=qSketchRegion(id+"F99",true);
            extrude(context, id + "F100", {"entities" : qUnion([Q0]), "depth" : 6.35 * mm});
        }
        {
            var Q0;
            Q0=makeQuery(id+"F100.opExtrude","SWEPT_BODY",BODY,{"disambiguationData":[OSD([sQuery(id+"F99.wireOp",EDGE,"E49")])]});
            var Q1;
            Q1=sQuery(id+"F0.wireOp",EDGE,"E0");
            circularPattern(context, id + "F101", {"entities" : qUnion([Q0]), "axis" : qUnion([Q1]), "angle" : 20 * degree, "instanceCount" : round(18)});
        }
        {
            var Q0;
            Q0=makeQuery(id+"F5.opPattern","COPY",EDGE,{"derivedFrom":makeQuery(id+"F4.opRevolve","CAP_EDGE",EDGE,{"disambiguationData":[OSD([sQuery(id+"F3.wireOp",EDGE,"E1.29")])],"isStart":true}),"instanceName":"13"});
            var Q1;
            Q1=sQuery(id+"F0.wireOp",EDGE,"E0");
            cPlane(context, id + "F102", {"entities" : qUnion([Q0, Q1]), "cplaneType" : CPlaneType.LINE_ANGLE, "offset" : 152.4 * mm, "angle" : 90 * degree, "width" : 152.4 * mm, "height" : 152.4 * mm});
        }
        {
            var Q0;
            Q0=qCreatedBy(id+"F102.planeOp",FACE);
            var sketch = newSketch(context, id + "F103", { "sketchPlane" : qUnion([Q0])});
            skCircle(sketch, "E51", {"center": v(-29.79, -38.88) * mm, "radius": 2.22 * mm});
            skCircle(sketch, "E52", {"center": v(-29.79, -38.88) * mm, "radius": 0.95 * mm});
            skSolve(sketch);
        }
        {
            var Q0;
            Q0=qSketchRegion(id+"F103",true);
            extrude(context, id + "F104", {"entities" : qUnion([Q0]), "depth" : 6.35 * mm});
        }
        {
            var Q0;
            Q0=makeQuery(id+"F104.opExtrude","SWEPT_BODY",BODY,{"disambiguationData":[OSD([sQuery(id+"F103.wireOp",EDGE,"E51")])]});
            var Q1;
            Q1=sQuery(id+"F0.wireOp",EDGE,"E0");
            circularPattern(context, id + "F105", {"entities" : qUnion([Q0]), "axis" : qUnion([Q1]), "angle" : 20 * degree, "instanceCount" : round(18)});
        }
        {
            var Q0;
            Q0=makeQuery(id+"F5.opPattern","COPY",EDGE,{"derivedFrom":makeQuery(id+"F4.opRevolve","CAP_EDGE",EDGE,{"disambiguationData":[OSD([sQuery(id+"F3.wireOp",EDGE,"E1.28")])],"isStart":false}),"instanceName":"13"});
            var Q1;
            Q1=sQuery(id+"F0.wireOp",EDGE,"E0");
            cPlane(context, id + "F106", {"entities" : qUnion([Q0, Q1]), "cplaneType" : CPlaneType.LINE_ANGLE, "offset" : 152.4 * mm, "angle" : 90 * degree, "width" : 152.4 * mm, "height" : 152.4 * mm});
        }
        {
            var Q0;
            Q0=qCreatedBy(id+"F106.planeOp",FACE);
            var sketch = newSketch(context, id + "F107", { "sketchPlane" : qUnion([Q0])});
            skCircle(sketch, "E53", {"center": v(-31.56, -49.1) * mm, "radius": 2.22 * mm});
            skCircle(sketch, "E54", {"center": v(-31.56, -49.1) * mm, "radius": 0.95 * mm});
            skSolve(sketch);
        }
        {
            var Q0;
            Q0=qSketchRegion(id+"F107",true);
            extrude(context, id + "F108", {"entities" : qUnion([Q0]), "depth" : 6.35 * mm});
        }
        {
            var Q0;
            Q0=makeQuery(id+"F108.opExtrude","SWEPT_BODY",BODY,{"disambiguationData":[OSD([sQuery(id+"F107.wireOp",EDGE,"E53")])]});
            var Q1;
            Q1=sQuery(id+"F0.wireOp",EDGE,"E0");
            circularPattern(context, id + "F109", {"entities" : qUnion([Q0]), "axis" : qUnion([Q1]), "angle" : 20 * degree, "instanceCount" : round(18)});
        }
        {
            var Q0;
            Q0=makeQuery(id+"F5.opPattern","COPY",EDGE,{"derivedFrom":makeQuery(id+"F4.opRevolve","CAP_EDGE",EDGE,{"disambiguationData":[OSD([sQuery(id+"F3.wireOp",EDGE,"E1.27")])],"isStart":true}),"instanceName":"11"});
            var Q1;
            Q1=sQuery(id+"F0.wireOp",EDGE,"E0");
            cPlane(context, id + "F110", {"entities" : qUnion([Q0, Q1]), "cplaneType" : CPlaneType.LINE_ANGLE, "offset" : 152.4 * mm, "angle" : 90 * degree, "width" : 152.4 * mm, "height" : 152.4 * mm});
        }
        {
            var Q0;
            Q0=qCreatedBy(id+"F110.planeOp",FACE);
            var sketch = newSketch(context, id + "F111", { "sketchPlane" : qUnion([Q0])});
            skCircle(sketch, "E55", {"center": v(-60.84, -25.57) * mm, "radius": 2.22 * mm});
            skCircle(sketch, "E56", {"center": v(-60.84, -25.57) * mm, "radius": 0.95 * mm});
            skSolve(sketch);
        }
        {
            var Q0;
            Q0=qSketchRegion(id+"F111",true);
            extrude(context, id + "F112", {"entities" : qUnion([Q0]), "depth" : 6.35 * mm});
        }
        {
            var Q0;
            Q0=makeQuery(id+"F112.opExtrude","SWEPT_BODY",BODY,{"disambiguationData":[OSD([sQuery(id+"F111.wireOp",EDGE,"E55")])]});
            var Q1;
            Q1=sQuery(id+"F0.wireOp",EDGE,"E0");
            circularPattern(context, id + "F113", {"entities" : qUnion([Q0]), "axis" : qUnion([Q1]), "angle" : 20 * degree, "instanceCount" : round(18)});
        }
        {
            var Q0;
            Q0=makeQuery(id+"F5.opPattern","COPY",EDGE,{"derivedFrom":makeQuery(id+"F4.opRevolve","CAP_EDGE",EDGE,{"disambiguationData":[OSD([sQuery(id+"F3.wireOp",EDGE,"E1.26")])],"isStart":true}),"instanceName":"30"});
            var Q1;
            Q1=sQuery(id+"F0.wireOp",EDGE,"E0");
            cPlane(context, id + "F114", {"entities" : qUnion([Q0, Q1]), "cplaneType" : CPlaneType.LINE_ANGLE, "offset" : 152.4 * mm, "angle" : 90 * degree, "width" : 152.4 * mm, "height" : 152.4 * mm});
        }
        {
            var Q0;
            Q0=qCreatedBy(id+"F114.planeOp",FACE);
            var sketch = newSketch(context, id + "F115", { "sketchPlane" : qUnion([Q0])});
            skCircle(sketch, "E57", {"center": v(61, 37.48) * mm, "radius": 2.22 * mm});
            skCircle(sketch, "E58", {"center": v(61, 37.48) * mm, "radius": 0.95 * mm});
            skSolve(sketch);
        }
        {
            var Q0;
            Q0=makeQuery(id+"F115.imprint","IMPRINT",FACE,{"disambiguationData":[TD([[makeQuery(id+"F115.imprint","IMPRINT",EDGE,{"derivedFrom":sQuery(id+"F115.wireOp",EDGE,"E57")}),1.0]])]});
            extrude(context, id + "F116", {"entities" : qUnion([Q0]), "depth" : 6.35 * mm});
        }
        {
            var Q0;
            Q0=makeQuery(id+"F116.opExtrude","SWEPT_BODY",BODY,{"disambiguationData":[OSD([sQuery(id+"F115.wireOp",EDGE,"E57")])]});
            var Q1;
            Q1=sQuery(id+"F0.wireOp",EDGE,"E0");
            circularPattern(context, id + "F117", {"entities" : qUnion([Q0]), "axis" : qUnion([Q1]), "angle" : 20 * degree, "instanceCount" : round(18)});
        }
        {
            var Q0;
            Q0=makeQuery(id+"F5.opPattern","COPY",EDGE,{"derivedFrom":makeQuery(id+"F4.opRevolve","CAP_EDGE",EDGE,{"disambiguationData":[OSD([sQuery(id+"F3.wireOp",EDGE,"E1.25")])],"isStart":false}),"instanceName":"6"});
            var Q1;
            Q1=sQuery(id+"F0.wireOp",EDGE,"E0");
            cPlane(context, id + "F118", {"entities" : qUnion([Q0, Q1]), "cplaneType" : CPlaneType.LINE_ANGLE, "offset" : 152.4 * mm, "angle" : 90 * degree, "width" : 152.4 * mm, "height" : 152.4 * mm});
        }
        {
            var Q0;
            Q0=qCreatedBy(id+"F118.planeOp",FACE);
            var sketch = newSketch(context, id + "F119", { "sketchPlane" : qUnion([Q0])});
            skCircle(sketch, "E59", {"center": v(-70.39, 26.01) * mm, "radius": 2.22 * mm});
            skCircle(sketch, "E60", {"center": v(-70.39, 26.01) * mm, "radius": 0.95 * mm});
            skSolve(sketch);
        }
        {
            var Q0;
            Q0=qSketchRegion(id+"F119",true);
            extrude(context, id + "F120", {"entities" : qUnion([Q0]), "depth" : 6.35 * mm});
        }
        {
            var Q0;
            Q0=makeQuery(id+"F120.opExtrude","SWEPT_BODY",BODY,{"disambiguationData":[OSD([sQuery(id+"F119.wireOp",EDGE,"E59")])]});
            var Q1;
            Q1=sQuery(id+"F0.wireOp",EDGE,"E0");
            circularPattern(context, id + "F121", {"entities" : qUnion([Q0]), "axis" : qUnion([Q1]), "angle" : 20 * degree, "instanceCount" : round(18)});
        }
        {
            var Q0;
            Q0=makeQuery(id+"F5.opPattern","COPY",EDGE,{"derivedFrom":makeQuery(id+"F4.opRevolve","CAP_EDGE",EDGE,{"disambiguationData":[OSD([sQuery(id+"F3.wireOp",EDGE,"E1.24")])],"isStart":false}),"instanceName":"5"});
            var Q1;
            Q1=sQuery(id+"F0.wireOp",EDGE,"E0");
            cPlane(context, id + "F122", {"entities" : qUnion([Q0, Q1]), "cplaneType" : CPlaneType.LINE_ANGLE, "offset" : 152.4 * mm, "angle" : 90 * degree, "width" : 152.4 * mm, "height" : 152.4 * mm});
        }
        {
            var Q0;
            Q0=qCreatedBy(id+"F122.planeOp",FACE);
            var sketch = newSketch(context, id + "F123", { "sketchPlane" : qUnion([Q0])});
            skCircle(sketch, "E61", {"center": v(-66, 38.1) * mm, "radius": 2.22 * mm});
            skCircle(sketch, "E62", {"center": v(-66, 38.1) * mm, "radius": 0.95 * mm});
            skSolve(sketch);
        }
        {
            var Q0;
            Q0=qSketchRegion(id+"F123",true);
            extrude(context, id + "F124", {"entities" : qUnion([Q0]), "depth" : 6.35 * mm});
        }
        {
            var Q0;
            Q0=makeQuery(id+"F124.opExtrude","SWEPT_BODY",BODY,{"disambiguationData":[OSD([sQuery(id+"F123.wireOp",EDGE,"E61")])]});
            var Q1;
            Q1=sQuery(id+"F0.wireOp",EDGE,"E0");
            circularPattern(context, id + "F125", {"entities" : qUnion([Q0]), "axis" : qUnion([Q1]), "angle" : 20 * degree, "instanceCount" : round(18)});
        }
        {
            var Q0;
            Q0=makeQuery(id+"F5.opPattern","COPY",EDGE,{"derivedFrom":makeQuery(id+"F4.opRevolve","CAP_EDGE",EDGE,{"disambiguationData":[OSD([sQuery(id+"F3.wireOp",EDGE,"E1.23")])],"isStart":false}),"instanceName":"6"});
            var Q1;
            Q1=sQuery(id+"F0.wireOp",EDGE,"E0");
            cPlane(context, id + "F126", {"entities" : qUnion([Q0, Q1]), "cplaneType" : CPlaneType.LINE_ANGLE, "offset" : 152.4 * mm, "angle" : 90 * degree, "width" : 152.4 * mm, "height" : 152.4 * mm});
        }
        {
            var Q0;
            Q0=qCreatedBy(id+"F126.planeOp",FACE);
            var sketch = newSketch(context, id + "F127", { "sketchPlane" : qUnion([Q0])});
            skCircle(sketch, "E63", {"center": v(-70.39, 26.01) * mm, "radius": 2.22 * mm});
            skCircle(sketch, "E64", {"center": v(-70.39, 26.01) * mm, "radius": 0.95 * mm});
            skSolve(sketch);
        }
        {
            var Q0;
            Q0=qSketchRegion(id+"F127",true);
            extrude(context, id + "F128", {"entities" : qUnion([Q0]), "depth" : 6.35 * mm});
        }
        {
            var Q0;
            Q0=makeQuery(id+"F128.opExtrude","SWEPT_BODY",BODY,{"disambiguationData":[OSD([sQuery(id+"F127.wireOp",EDGE,"E63")])]});
            var Q1;
            Q1=sQuery(id+"F0.wireOp",EDGE,"E0");
            circularPattern(context, id + "F129", {"entities" : qUnion([Q0]), "axis" : qUnion([Q1]), "angle" : 20 * degree, "instanceCount" : round(18)});
        }
        {
            var Q0;
            Q0=makeQuery(id+"F5.opPattern","COPY",EDGE,{"derivedFrom":makeQuery(id+"F4.opRevolve","CAP_EDGE",EDGE,{"disambiguationData":[OSD([sQuery(id+"F3.wireOp",EDGE,"E1.22")])],"isStart":false}),"instanceName":"7"});
            var Q1;
            Q1=sQuery(id+"F0.wireOp",EDGE,"E0");
            cPlane(context, id + "F130", {"entities" : qUnion([Q0, Q1]), "cplaneType" : CPlaneType.LINE_ANGLE, "offset" : 152.4 * mm, "angle" : 90 * degree, "width" : 152.4 * mm, "height" : 152.4 * mm});
        }
        {
            var Q0;
            Q0=qCreatedBy(id+"F130.planeOp",FACE);
            var sketch = newSketch(context, id + "F131", { "sketchPlane" : qUnion([Q0])});
            skCircle(sketch, "E65", {"center": v(-70.38, 13.2) * mm, "radius": 2.22 * mm});
            skCircle(sketch, "E66", {"center": v(-70.38, 13.2) * mm, "radius": 0.95 * mm});
            skSolve(sketch);
        }
        {
            var Q0;
            Q0=qSketchRegion(id+"F131",true);
            extrude(context, id + "F132", {"entities" : qUnion([Q0]), "depth" : 6.35 * mm});
        }
        {
            var Q0;
            Q0=makeQuery(id+"F132.opExtrude","SWEPT_BODY",BODY,{"disambiguationData":[OSD([sQuery(id+"F131.wireOp",EDGE,"E65")])]});
            var Q1;
            Q1=sQuery(id+"F0.wireOp",EDGE,"E0");
            circularPattern(context, id + "F133", {"entities" : qUnion([Q0]), "axis" : qUnion([Q1]), "angle" : 20 * degree, "instanceCount" : round(18)});
        }
        {
            var Q0;
            Q0=makeQuery(id+"F5.opPattern","COPY",EDGE,{"derivedFrom":makeQuery(id+"F4.opRevolve","CAP_EDGE",EDGE,{"disambiguationData":[OSD([sQuery(id+"F3.wireOp",EDGE,"E1.21")])],"isStart":false}),"instanceName":"8"});
            var Q1;
            Q1=sQuery(id+"F0.wireOp",EDGE,"E0");
            cPlane(context, id + "F134", {"entities" : qUnion([Q0, Q1]), "cplaneType" : CPlaneType.LINE_ANGLE, "offset" : 152.4 * mm, "angle" : 90 * degree, "width" : 152.4 * mm, "height" : 152.4 * mm});
        }
        {
            var Q0;
            Q0=qCreatedBy(id+"F134.planeOp",FACE);
            var sketch = newSketch(context, id + "F135", { "sketchPlane" : qUnion([Q0])});
            skCircle(sketch, "E67", {"center": v(-66, 0) * mm, "radius": 2.22 * mm});
            skCircle(sketch, "E68", {"center": v(-66, 0) * mm, "radius": 0.95 * mm});
            skSolve(sketch);
        }
        {
            var Q0;
            Q0=qSketchRegion(id+"F135",true);
            extrude(context, id + "F136", {"entities" : qUnion([Q0]), "depth" : 6.35 * mm});
        }
        {
            var Q0;
            Q0=makeQuery(id+"F136.opExtrude","SWEPT_BODY",BODY,{"disambiguationData":[OSD([sQuery(id+"F135.wireOp",EDGE,"E67")])]});
            var Q1;
            Q1=sQuery(id+"F0.wireOp",EDGE,"E0");
            circularPattern(context, id + "F137", {"entities" : qUnion([Q0]), "axis" : qUnion([Q1]), "angle" : 20 * degree, "instanceCount" : round(18)});
        }
        {
            var Q0;
            Q0=makeQuery(id+"F5.opPattern","COPY",EDGE,{"derivedFrom":makeQuery(id+"F4.opRevolve","CAP_EDGE",EDGE,{"disambiguationData":[OSD([sQuery(id+"F3.wireOp",EDGE,"E1.20")])],"isStart":false}),"instanceName":"7"});
            var Q1;
            Q1=sQuery(id+"F0.wireOp",EDGE,"E0");
            cPlane(context, id + "F138", {"entities" : qUnion([Q0, Q1]), "cplaneType" : CPlaneType.LINE_ANGLE, "offset" : 152.4 * mm, "angle" : 90 * degree, "width" : 152.4 * mm, "height" : 152.4 * mm});
        }
        {
            var Q0;
            Q0=qCreatedBy(id+"F138.planeOp",FACE);
            var sketch = newSketch(context, id + "F139", { "sketchPlane" : qUnion([Q0])});
            skCircle(sketch, "E69", {"center": v(-56.89, 13.1) * mm, "radius": 2.22 * mm});
            skCircle(sketch, "E70", {"center": v(-56.89, 13.1) * mm, "radius": 0.95 * mm});
            skSolve(sketch);
        }
        {
            var Q0;
            Q0=qSketchRegion(id+"F139",true);
            extrude(context, id + "F140", {"entities" : qUnion([Q0]), "depth" : 6.35 * mm});
        }
        {
            var Q0;
            Q0=makeQuery(id+"F140.opExtrude","SWEPT_BODY",BODY,{"disambiguationData":[OSD([sQuery(id+"F139.wireOp",EDGE,"E69")])]});
            var Q1;
            Q1=sQuery(id+"F0.wireOp",EDGE,"E0");
            circularPattern(context, id + "F141", {"entities" : qUnion([Q0]), "axis" : qUnion([Q1]), "angle" : 20 * degree, "instanceCount" : round(18)});
        }
        {
            var Q0;
            Q0=makeQuery(id+"F5.opPattern","COPY",EDGE,{"derivedFrom":makeQuery(id+"F4.opRevolve","CAP_EDGE",EDGE,{"disambiguationData":[OSD([sQuery(id+"F3.wireOp",EDGE,"E1.19")])],"isStart":false}),"instanceName":"6"});
            var Q1;
            Q1=sQuery(id+"F0.wireOp",EDGE,"E0");
            cPlane(context, id + "F142", {"entities" : qUnion([Q0, Q1]), "cplaneType" : CPlaneType.LINE_ANGLE, "offset" : 152.4 * mm, "angle" : 90 * degree, "width" : 152.4 * mm, "height" : 152.4 * mm});
        }
        {
            var Q0;
            Q0=qCreatedBy(id+"F142.planeOp",FACE);
            var sketch = newSketch(context, id + "F143", { "sketchPlane" : qUnion([Q0])});
            skCircle(sketch, "E71", {"center": v(-11.16, -47.7) * mm, "radius": 2.22 * mm});
            skCircle(sketch, "E72", {"center": v(-11.16, -47.7) * mm, "radius": 0.95 * mm});
            skSolve(sketch);
        }
        {
            var Q0;
            Q0=qSketchRegion(id+"F143",true);
            extrude(context, id + "F144", {"entities" : qUnion([Q0]), "depth" : 6.35 * mm});
        }
        {
            var Q0;
            Q0=makeQuery(id+"F144.opExtrude","SWEPT_BODY",BODY,{"disambiguationData":[OSD([sQuery(id+"F143.wireOp",EDGE,"E71")])]});
            var Q1;
            Q1=sQuery(id+"F0.wireOp",EDGE,"E0");
            circularPattern(context, id + "F145", {"entities" : qUnion([Q0]), "axis" : qUnion([Q1]), "angle" : 20 * degree, "instanceCount" : round(18)});
        }
        {
            var Q0;
            Q0=makeQuery(id+"F5.opPattern","COPY",EDGE,{"derivedFrom":makeQuery(id+"F4.opRevolve","CAP_EDGE",EDGE,{"disambiguationData":[OSD([sQuery(id+"F3.wireOp",EDGE,"E1.18")])],"isStart":false}),"instanceName":"7"});
            var Q1;
            Q1=sQuery(id+"F0.wireOp",EDGE,"E0");
            cPlane(context, id + "F146", {"entities" : qUnion([Q0, Q1]), "cplaneType" : CPlaneType.LINE_ANGLE, "offset" : 152.4 * mm, "angle" : 90 * degree, "width" : 152.4 * mm, "height" : 152.4 * mm});
        }
        {
            var Q0;
            Q0=qCreatedBy(id+"F146.planeOp",FACE);
            var sketch = newSketch(context, id + "F147", { "sketchPlane" : qUnion([Q0])});
            skCircle(sketch, "E73", {"center": v(-3.35, -37.95) * mm, "radius": 2.22 * mm});
            skCircle(sketch, "E74", {"center": v(-3.35, -37.95) * mm, "radius": 0.95 * mm});
            skSolve(sketch);
        }
        {
            var Q0;
            Q0=qSketchRegion(id+"F147",true);
            extrude(context, id + "F148", {"entities" : qUnion([Q0]), "depth" : 6.35 * mm});
        }
        {
            var Q0;
            Q0=makeQuery(id+"F148.opExtrude","SWEPT_BODY",BODY,{"disambiguationData":[OSD([sQuery(id+"F147.wireOp",EDGE,"E73")])]});
            var Q1;
            Q1=sQuery(id+"F0.wireOp",EDGE,"E0");
            circularPattern(context, id + "F149", {"entities" : qUnion([Q0]), "axis" : qUnion([Q1]), "angle" : 20 * degree, "instanceCount" : round(18)});
        }
        {
            var Q0;
            Q0=makeQuery(id+"F5.opPattern","COPY",EDGE,{"derivedFrom":makeQuery(id+"F4.opRevolve","CAP_EDGE",EDGE,{"disambiguationData":[OSD([sQuery(id+"F3.wireOp",EDGE,"E1.33")])],"isStart":true}),"instanceName":"18"});
            var Q1;
            Q1=sQuery(id+"F0.wireOp",EDGE,"E0");
            cPlane(context, id + "F150", {"entities" : qUnion([Q0, Q1]), "cplaneType" : CPlaneType.LINE_ANGLE, "offset" : 152.4 * mm, "angle" : 90 * degree, "width" : 152.4 * mm, "height" : 152.4 * mm});
        }
        {
            var Q0;
            Q0=qCreatedBy(id+"F150.planeOp",FACE);
            var sketch = newSketch(context, id + "F151", { "sketchPlane" : qUnion([Q0])});
            skCircle(sketch, "E75", {"center": v(0, 0) * mm, "radius": 2.22 * mm});
            skSolve(sketch);
        }
        {
            var Q0;
            Q0=makeQuery(id+"F151.imprint","IMPRINT",FACE,{"disambiguationData":[TD([[makeQuery(id+"F151.imprint","IMPRINT",EDGE,{"derivedFrom":sQuery(id+"F151.wireOp",EDGE,"E75")}),1.0]])]});
            extrude(context, id + "F152", {"entities" : qUnion([Q0]), "operationType" : NewBodyOperationType.REMOVE, "oppositeDirection" : true, "depth" : 6.35 * mm});
        }
        {
            var Q0;
            Q0=qSketchRegion(id+"F7",true);
            extrude(context, id + "F153", {"entities" : qUnion([Q0]), "operationType" : NewBodyOperationType.ADD, "depth" : 2.54 * mm});
        }
        {
            var Q0;
            Q0=qSketchRegion(id+"F11",true);
            extrude(context, id + "F154", {"entities" : qUnion([Q0]), "operationType" : NewBodyOperationType.ADD, "depth" : 2.54 * mm});
        }
        {
            var Q0;
            Q0=qSketchRegion(id+"F15",true);
            extrude(context, id + "F155", {"entities" : qUnion([Q0]), "operationType" : NewBodyOperationType.ADD, "depth" : 2.54 * mm});
        }
        {
            var Q0;
            Q0=qSketchRegion(id+"F19",true);
            extrude(context, id + "F156", {"entities" : qUnion([Q0]), "operationType" : NewBodyOperationType.ADD, "depth" : 2.54 * mm});
        }
        {
            var Q0;
            Q0=qSketchRegion(id+"F23",true);
            extrude(context, id + "F157", {"entities" : qUnion([Q0]), "operationType" : NewBodyOperationType.ADD, "depth" : 2.54 * mm});
        }
        {
            var Q0;
            Q0=qSketchRegion(id+"F27",true);
            extrude(context, id + "F158", {"entities" : qUnion([Q0]), "operationType" : NewBodyOperationType.ADD, "depth" : 2.54 * mm});
        }
        {
            var Q0;
            Q0=qSketchRegion(id+"F31",true);
            extrude(context, id + "F159", {"entities" : qUnion([Q0]), "operationType" : NewBodyOperationType.ADD, "depth" : 2.54 * mm});
        }
        {
            var Q0;
            Q0=qSketchRegion(id+"F35",true);
            extrude(context, id + "F160", {"entities" : qUnion([Q0]), "operationType" : NewBodyOperationType.ADD, "depth" : 2.54 * mm});
        }
        {
            var Q0;
            Q0=qSketchRegion(id+"F39",true);
            extrude(context, id + "F161", {"entities" : qUnion([Q0]), "operationType" : NewBodyOperationType.ADD, "depth" : 2.54 * mm});
        }
        {
            var Q0;
            Q0=qSketchRegion(id+"F43",true);
            extrude(context, id + "F162", {"entities" : qUnion([Q0]), "operationType" : NewBodyOperationType.ADD, "depth" : 2.54 * mm});
        }
        {
            var Q0;
            Q0=qSketchRegion(id+"F47",true);
            extrude(context, id + "F163", {"entities" : qUnion([Q0]), "operationType" : NewBodyOperationType.ADD, "depth" : 2.54 * mm});
        }
        {
            var Q0;
            Q0=qSketchRegion(id+"F51",true);
            extrude(context, id + "F164", {"entities" : qUnion([Q0]), "operationType" : NewBodyOperationType.ADD, "depth" : 2.54 * mm});
        }
        {
            var Q0;
            Q0=qSketchRegion(id+"F55",true);
            extrude(context, id + "F165", {"entities" : qUnion([Q0]), "operationType" : NewBodyOperationType.ADD, "depth" : 2.8 * mm});
        }
        {
            var Q0;
            Q0=qSketchRegion(id+"F59",true);
            extrude(context, id + "F166", {"entities" : qUnion([Q0]), "operationType" : NewBodyOperationType.ADD, "depth" : 2.54 * mm});
        }
        {
            var Q0;
            Q0=qSketchRegion(id+"F63",true);
            extrude(context, id + "F167", {"entities" : qUnion([Q0]), "operationType" : NewBodyOperationType.ADD, "depth" : 2.54 * mm});
        }
        {
            var Q0;
            Q0=qSketchRegion(id+"F67",true);
            extrude(context, id + "F168", {"entities" : qUnion([Q0]), "operationType" : NewBodyOperationType.ADD, "depth" : 2.54 * mm});
        }
        {
            var Q0;
            Q0=qSketchRegion(id+"F71",true);
            extrude(context, id + "F169", {"entities" : qUnion([Q0]), "operationType" : NewBodyOperationType.ADD, "depth" : 2.54 * mm});
        }
        {
            var Q0;
            Q0=qSketchRegion(id+"F75",true);
            extrude(context, id + "F170", {"entities" : qUnion([Q0]), "operationType" : NewBodyOperationType.ADD, "depth" : 2.54 * mm});
        }
        {
            var Q0;
            Q0=qSketchRegion(id+"F79",true);
            extrude(context, id + "F171", {"entities" : qUnion([Q0]), "operationType" : NewBodyOperationType.ADD, "oppositeDirection" : true, "depth" : 2.54 * mm});
        }
        {
            var Q0;
            Q0=qSketchRegion(id+"F83",true);
            extrude(context, id + "F172", {"entities" : qUnion([Q0]), "operationType" : NewBodyOperationType.ADD, "oppositeDirection" : true, "depth" : 2.54 * mm});
        }
        {
            var Q0;
            Q0=qSketchRegion(id+"F87",true);
            extrude(context, id + "F173", {"entities" : qUnion([Q0]), "operationType" : NewBodyOperationType.ADD, "oppositeDirection" : true, "depth" : 2.54 * mm});
        }
        {
            var Q0;
            Q0=qSketchRegion(id+"F91",true);
            extrude(context, id + "F174", {"entities" : qUnion([Q0]), "operationType" : NewBodyOperationType.ADD, "oppositeDirection" : true, "depth" : 2.54 * mm});
        }
        {
            var Q0;
            Q0=qSketchRegion(id+"F95",true);
            extrude(context, id + "F175", {"entities" : qUnion([Q0]), "operationType" : NewBodyOperationType.ADD, "oppositeDirection" : true, "depth" : 2.54 * mm});
        }
        {
            var Q0;
            Q0=qSketchRegion(id+"F99",true);
            extrude(context, id + "F176", {"entities" : qUnion([Q0]), "operationType" : NewBodyOperationType.ADD, "oppositeDirection" : true, "depth" : 2.54 * mm});
        }
        {
            var Q0;
            Q0=qSketchRegion(id+"F103",true);
            extrude(context, id + "F177", {"entities" : qUnion([Q0]), "operationType" : NewBodyOperationType.ADD, "oppositeDirection" : true, "depth" : 2.54 * mm});
        }
        {
            var Q0;
            Q0=qSketchRegion(id+"F107",true);
            extrude(context, id + "F178", {"entities" : qUnion([Q0]), "operationType" : NewBodyOperationType.ADD, "oppositeDirection" : true, "depth" : 2.54 * mm});
        }
        {
            var Q0;
            Q0=qSketchRegion(id+"F111",true);
            extrude(context, id + "F179", {"entities" : qUnion([Q0]), "operationType" : NewBodyOperationType.ADD, "oppositeDirection" : true, "depth" : 2.54 * mm});
        }
        {
            var Q0;
            Q0=qSketchRegion(id+"F115",true);
            extrude(context, id + "F180", {"entities" : qUnion([Q0]), "operationType" : NewBodyOperationType.ADD, "oppositeDirection" : true, "depth" : 2.54 * mm});
        }
        {
            var Q0;
            Q0=qSketchRegion(id+"F119",true);
            extrude(context, id + "F181", {"entities" : qUnion([Q0]), "operationType" : NewBodyOperationType.ADD, "oppositeDirection" : true, "depth" : 2.54 * mm});
        }
        {
            var Q0;
            Q0=qSketchRegion(id+"F123",true);
            extrude(context, id + "F182", {"entities" : qUnion([Q0]), "operationType" : NewBodyOperationType.ADD, "oppositeDirection" : true, "depth" : 2.54 * mm});
        }
        {
            var Q0;
            Q0=qSketchRegion(id+"F127",true);
            extrude(context, id + "F183", {"entities" : qUnion([Q0]), "operationType" : NewBodyOperationType.ADD, "oppositeDirection" : true, "depth" : 2.54 * mm});
        }
        {
            var Q0;
            Q0=qSketchRegion(id+"F131",true);
            extrude(context, id + "F184", {"entities" : qUnion([Q0]), "operationType" : NewBodyOperationType.ADD, "oppositeDirection" : true, "depth" : 2.54 * mm});
        }
        {
            var Q0;
            Q0=qSketchRegion(id+"F135",true);
            extrude(context, id + "F185", {"entities" : qUnion([Q0]), "operationType" : NewBodyOperationType.ADD, "oppositeDirection" : true, "depth" : 2.54 * mm});
        }
        {
            var Q0;
            Q0=qSketchRegion(id+"F139",true);
            extrude(context, id + "F186", {"entities" : qUnion([Q0]), "operationType" : NewBodyOperationType.ADD, "oppositeDirection" : true, "depth" : 2.54 * mm});
        }
        {
            var Q0;
            Q0=qSketchRegion(id+"F143",true);
            extrude(context, id + "F187", {"entities" : qUnion([Q0]), "operationType" : NewBodyOperationType.ADD, "oppositeDirection" : true, "depth" : 2.54 * mm});
        }
        {
            var Q0;
            Q0=qSketchRegion(id+"F147",true);
            extrude(context, id + "F188", {"entities" : qUnion([Q0]), "operationType" : NewBodyOperationType.ADD, "oppositeDirection" : true, "depth" : 2.54 * mm});
        }
    });
